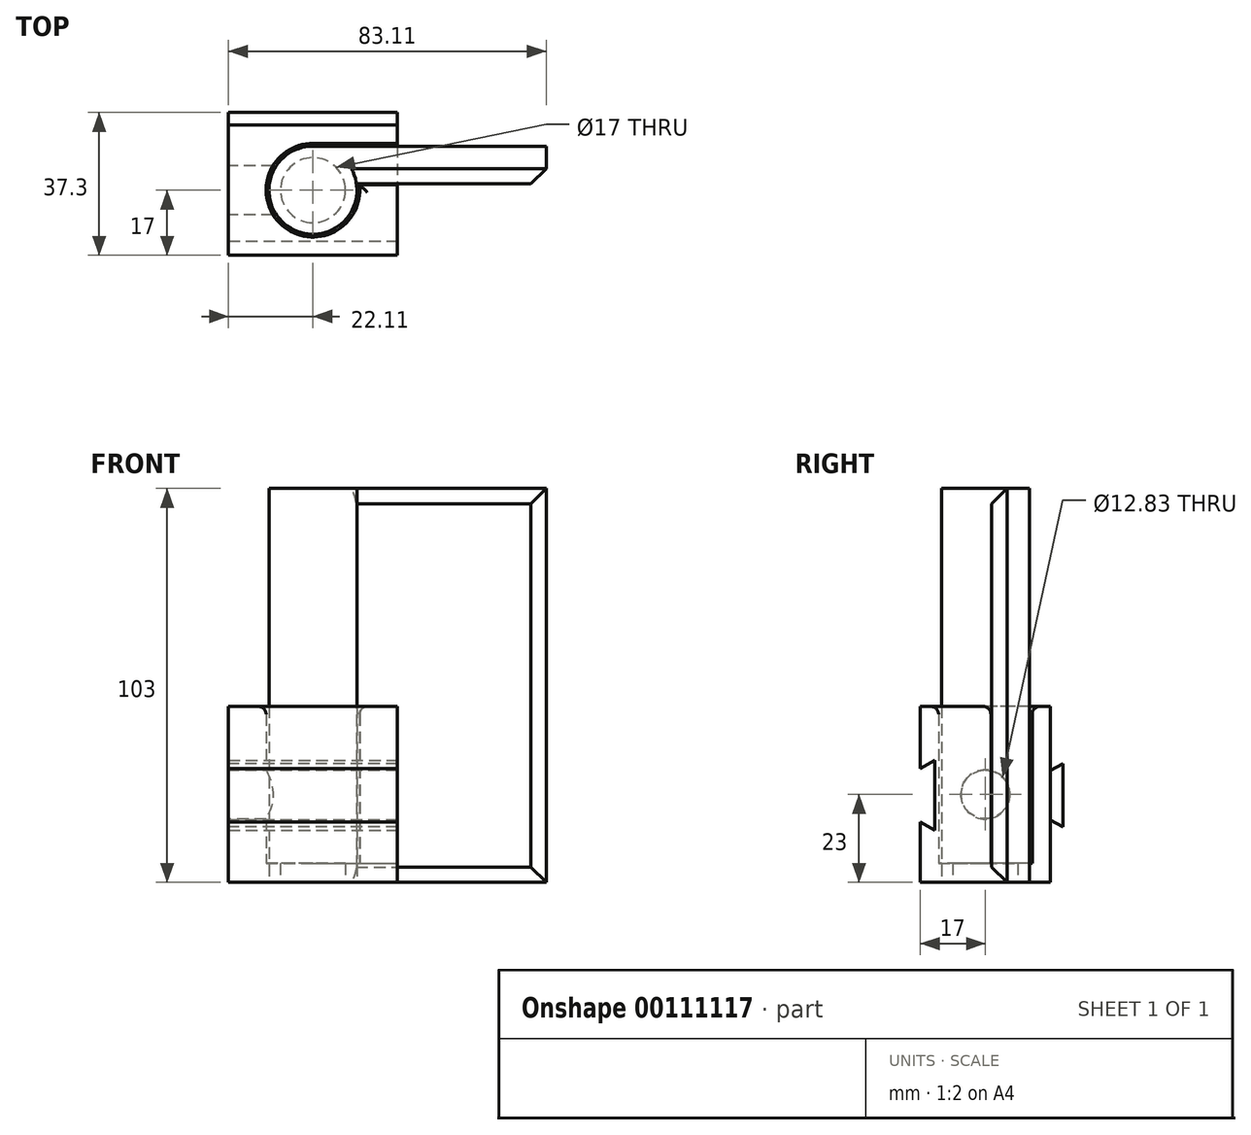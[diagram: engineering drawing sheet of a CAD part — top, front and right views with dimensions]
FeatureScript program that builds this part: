
annotation { "Feature Type Name" : "Feature", "Feature Type Description" : "" }
export const myFeature = defineFeature(function(context is Context, id is Id, definition is map)
    precondition{}
    {
        {
            var Q0;
            Q0=qCreatedBy(makeId("Top.planeOp"),FACE);
            var sketch = newSketch(context, id + "F0", { "sketchPlane" : qUnion([Q0])});
            skCircle(sketch, "E0", {"center": v(0, 0) * mm, "radius": 11.5 * mm});
            skLineSegment(sketch, "E1", {"start": v(0, 11.5) * mm, "end": v(0, -11.5) * mm, "construction": true});
            skLineSegment(sketch, "E2.bottom", {"start": v(0, 11.5) * mm, "end": v(61, 11.5) * mm});
            skLineSegment(sketch, "E2.top", {"start": v(0, 1.65) * mm, "end": v(61, 1.65) * mm});
            skLineSegment(sketch, "E2.left", {"start": v(0, 11.5) * mm, "end": v(0, 1.65) * mm});
            skLineSegment(sketch, "E2.right", {"start": v(61, 11.5) * mm, "end": v(61, 1.65) * mm});
            skSolve(sketch);
        }
        {
            var Q0;
            {var subQ0=sQuery(id+"F0.wireOp",EDGE,"E2.left");Q0=makeQuery(id+"F0.imprint","IMPRINT",FACE,{"disambiguationData":[TD([[makeQuery(id+"F0.imprint","IMPRINT",EDGE,{"derivedFrom":subQ0}),-1.0]])]});}
            var Q1;
            {var subQ0=sQuery(id+"F0.wireOp",EDGE,"E2.left");Q1=makeQuery(id+"F0.imprint","IMPRINT",FACE,{"disambiguationData":[TD([[makeQuery(id+"F0.imprint","IMPRINT",EDGE,{"derivedFrom":subQ0}),1.0]])]});}
            var Q2;
            {var subQ0=sQuery(id+"F0.wireOp",EDGE,"E2.bottom");Q2=makeQuery(id+"F0.imprint","IMPRINT",FACE,{"disambiguationData":[TD([[makeQuery(id+"F0.imprint","IMPRINT",EDGE,{"derivedFrom":subQ0}),-1.0]])]});}
            extrude(context, id + "F1", {"entities" : qUnion([Q0, Q1, Q2]), "depth" : 103 * mm});
        }
        {
            var Q0;
            Q0=makeQuery(id+"F1.opExtrude","CAP_EDGE",EDGE,{"disambiguationData":[OSD([sQuery(id+"F0.wireOp",EDGE,"E2.top")])],"isStart":false});
            var Q1;
            Q1=makeQuery(id+"F1.opExtrude","SWEPT_EDGE",EDGE,{"disambiguationData":[OSD([sQuery(id+"F0.wireOp",EDGE,"E2.top"),sQuery(id+"F0.wireOp",EDGE,"E2.right")])]});
            var Q2;
            Q2=makeQuery(id+"F1.opExtrude","CAP_EDGE",EDGE,{"disambiguationData":[OSD([sQuery(id+"F0.wireOp",EDGE,"E2.top")])],"isStart":true});
            chamfer(context, id + "F2", {"entities" : qUnion([Q0, Q1, Q2]), "width" : 4 * mm, "tangentPropagation" : true});
        }
        {
            var Q0;
            Q0=qCreatedBy(makeId("Top.planeOp"),FACE);
            var sketch = newSketch(context, id + "F3", { "sketchPlane" : qUnion([Q0])});
            skLineSegment(sketch, "E3.bottom", {"start": v(-22.1, 17) * mm, "end": v(22.1, 17) * mm});
            skLineSegment(sketch, "E3.top", {"start": v(-22.1, -17) * mm, "end": v(22.1, -17) * mm});
            skLineSegment(sketch, "E3.left", {"start": v(-22.1, 17) * mm, "end": v(-22.1, -17) * mm});
            skLineSegment(sketch, "E3.right", {"start": v(22.1, 17) * mm, "end": v(22.1, -17) * mm});
            skPoint(sketch, "E3.middle", {"position": v(0, 0) * mm});
            skCircle(sketch, "E4", {"center": v(0, 0) * mm, "radius": 12.25 * mm});
            skCircle(sketch, "E5", {"center": v(0, 0) * mm, "radius": 8.5 * mm});
            skLineSegment(sketch, "E6.bottom", {"start": v(0, 12.25) * mm, "end": v(22.1, 12.25) * mm});
            skLineSegment(sketch, "E6.top", {"start": v(12.16, 1.45) * mm, "end": v(22.1, 1.45) * mm});
            skLineSegment(sketch, "E7", {"start": v(0, -12.25) * mm, "end": v(0, 12.25) * mm, "construction": true});
            skSolve(sketch);
        }
        {
            var Q0;
            Q0=makeQuery(id+"F3.imprint","IMPRINT",FACE,{"disambiguationData":[TD([[makeQuery(id+"F3.imprint","IMPRINT",EDGE,{"derivedFrom":sQuery(id+"F3.wireOp",EDGE,"E4")}),1.0]])]});
            var Q1;
            {var subQ3=sQuery(id+"F3.wireOp",EDGE,"E6.top");var subQ5=sQuery(id+"F3.wireOp",EDGE,"E5");var subQ6=makeQuery(id+"F3.imprint","INTERSECT",VERTEX,{"derivedFrom":[subQ5,subQ3]});Q1=makeQuery(id+"F3.imprint","IMPRINT",FACE,{"disambiguationData":[TD([[makeQuery(id+"F3.imprint","IMPRINT",EDGE,{"disambiguationData":[TD([[subQ6,1.0]])],"derivedFrom":subQ5}),-1.0]])]});}
            var Q2;
            {var subQ1=sQuery(id+"F3.wireOp",EDGE,"E4");var subQ7=sQuery(id+"F3.wireOp",EDGE,"E6.bottom");var subQ9=makeQuery(id+"F3.imprint","INTERSECT",VERTEX,{"derivedFrom":[subQ1,subQ7]});Q2=makeQuery(id+"F3.imprint","IMPRINT",FACE,{"disambiguationData":[TD([[makeQuery(id+"F3.imprint","IMPRINT",EDGE,{"disambiguationData":[TD([[subQ9,1.0]])],"derivedFrom":subQ1}),1.0]])]});}
            var Q3;
            {var subQ0=sQuery(id+"F3.wireOp",EDGE,"E6.bottom");var subQ1=sQuery(id+"F3.wireOp",EDGE,"E3.right");var subQ2=makeQuery(id+"F3.imprint","INTERSECT",VERTEX,{"derivedFrom":[subQ1,subQ0]});Q3=makeQuery(id+"F3.imprint","IMPRINT",FACE,{"disambiguationData":[TD([[makeQuery(id+"F3.imprint","IMPRINT",EDGE,{"disambiguationData":[TD([[subQ2,-1.0]])],"derivedFrom":subQ1}),-1.0]])]});}
            extrude(context, id + "F4", {"entities" : qUnion([Q0, Q1, Q2, Q3]), "depth" : 5 * mm});
        }
        {
            var Q0;
            Q0=makeQuery(id+"F3.imprint","IMPRINT",FACE,{"disambiguationData":[TD([[makeQuery(id+"F3.imprint","IMPRINT",EDGE,{"derivedFrom":sQuery(id+"F3.wireOp",EDGE,"E3.bottom")}),-1.0]])]});
            extrude(context, id + "F5", {"entities" : qUnion([Q0]), "operationType" : NewBodyOperationType.ADD, "depth" : 46 * mm});
        }
        {
            var Q0;
            Q0=makeQuery(id+"F5.opExtrude","CAP_EDGE",EDGE,{"disambiguationData":[OSD([sQuery(id+"F3.wireOp",EDGE,"E4")])],"isStart":false});
            var Q1;
            Q1=makeQuery(id+"F5.opExtrude","CAP_EDGE",EDGE,{"disambiguationData":[OSD([sQuery(id+"F3.wireOp",EDGE,"E6.bottom")])],"isStart":false});
            var Q2;
            Q2=makeQuery(id+"F5.opExtrude","CAP_EDGE",EDGE,{"disambiguationData":[OSD([sQuery(id+"F3.wireOp",EDGE,"E6.top")])],"isStart":false});
            fillet(context, id + "F6", {"entities" : qUnion([Q0, Q1, Q2]), "radius" : 2 * mm, "tangentPropagation" : true, "allowEdgeOverflow" : false});
        }
        {
            var Q0;
            Q0=qCreatedBy(makeId("Right.planeOp"),FACE);
            var sketch = newSketch(context, id + "F7", { "sketchPlane" : qUnion([Q0])});
            skLineSegment(sketch, "E8", {"start": v(-17, 15.8) * mm, "end": v(-13.28, 13.65) * mm});
            skLineSegment(sketch, "E9", {"start": v(-13.28, 13.65) * mm, "end": v(-13.28, 31.95) * mm});
            skLineSegment(sketch, "E10", {"start": v(-13.28, 31.95) * mm, "end": v(-17, 29.8) * mm});
            skLineSegment(sketch, "E11", {"start": v(-17, 29.8) * mm, "end": v(-17, 15.8) * mm});
            skLineSegment(sketch, "E12", {"start": v(17, 16.28) * mm, "end": v(20.3, 14.56) * mm});
            skLineSegment(sketch, "E13", {"start": v(20.3, 14.56) * mm, "end": v(20.3, 31) * mm});
            skLineSegment(sketch, "E14", {"start": v(20.3, 31) * mm, "end": v(17, 29.28) * mm});
            skLineSegment(sketch, "E15", {"start": v(17, 29.28) * mm, "end": v(17, 16.28) * mm});
            skSolve(sketch);
        }
        {
            var Q0;
            Q0 = qSketchRegion(id + "F7", true);
            extrude(context, id + "F8", {"entities" : qUnion([Q0]), "operationType" : NewBodyOperationType.REMOVE, "oppositeDirection" : true, "depth" : 25 * mm, "hasSecondDirection" : true, "secondDirectionOppositeDirection" : false, "secondDirectionDepth" : 25 * mm});
        }
        {
            var Q0;
            Q0=makeQuery(id+"F7.imprint","IMPRINT",FACE,{"disambiguationData":[TD([[makeQuery(id+"F7.imprint","IMPRINT",EDGE,{"derivedFrom":sQuery(id+"F7.wireOp",EDGE,"E12")}),1.0]])]});
            extrude(context, id + "F9", {"entities" : qUnion([Q0]), "depth" : 22.1 * mm, "hasSecondDirection" : true, "secondDirectionOppositeDirection" : true, "secondDirectionDepth" : 22.1 * mm});
        }
        {
            var Q0;
            Q0=makeQuery(id+"F5.opExtrude","SWEPT_FACE",FACE,{"disambiguationData":[OSD([sQuery(id+"F3.wireOp",EDGE,"E3.left")])]});
            var sketch = newSketch(context, id + "F10", { "sketchPlane" : qUnion([Q0])});
            skLineSegment(sketch, "E16", {"start": v(-17, 0) * mm, "end": v(17, 46) * mm, "construction": true});
            skLineSegment(sketch, "E17", {"start": v(17, 0) * mm, "end": v(-17, 46) * mm, "construction": true});
            skCircle(sketch, "E18", {"center": v(0, 23) * mm, "radius": 6.41 * mm});
            skSolve(sketch);
        }
        {
            var Q0;
            Q0=makeQuery(id+"F10.imprint","IMPRINT",FACE,{"disambiguationData":[TD([[makeQuery(id+"F10.imprint","IMPRINT",EDGE,{"derivedFrom":sQuery(id+"F10.wireOp",EDGE,"E18")}),1.0]])]});
            var Q1;
            Q1=makeQuery(id+"F5.opExtrude","SWEPT_FACE",FACE,{"disambiguationData":[OSD([sQuery(id+"F3.wireOp",EDGE,"E4")])]});
            extrude(context, id + "F11", {"entities" : qUnion([Q0]), "operationType" : NewBodyOperationType.REMOVE, "endBound" : BoundingType.UP_TO_SURFACE, "oppositeDirection" : true, "depth" : 25 * mm, "endBoundEntityFace" : qUnion([Q1]), "offsetDistance" : 25 * mm});
        }
    });
